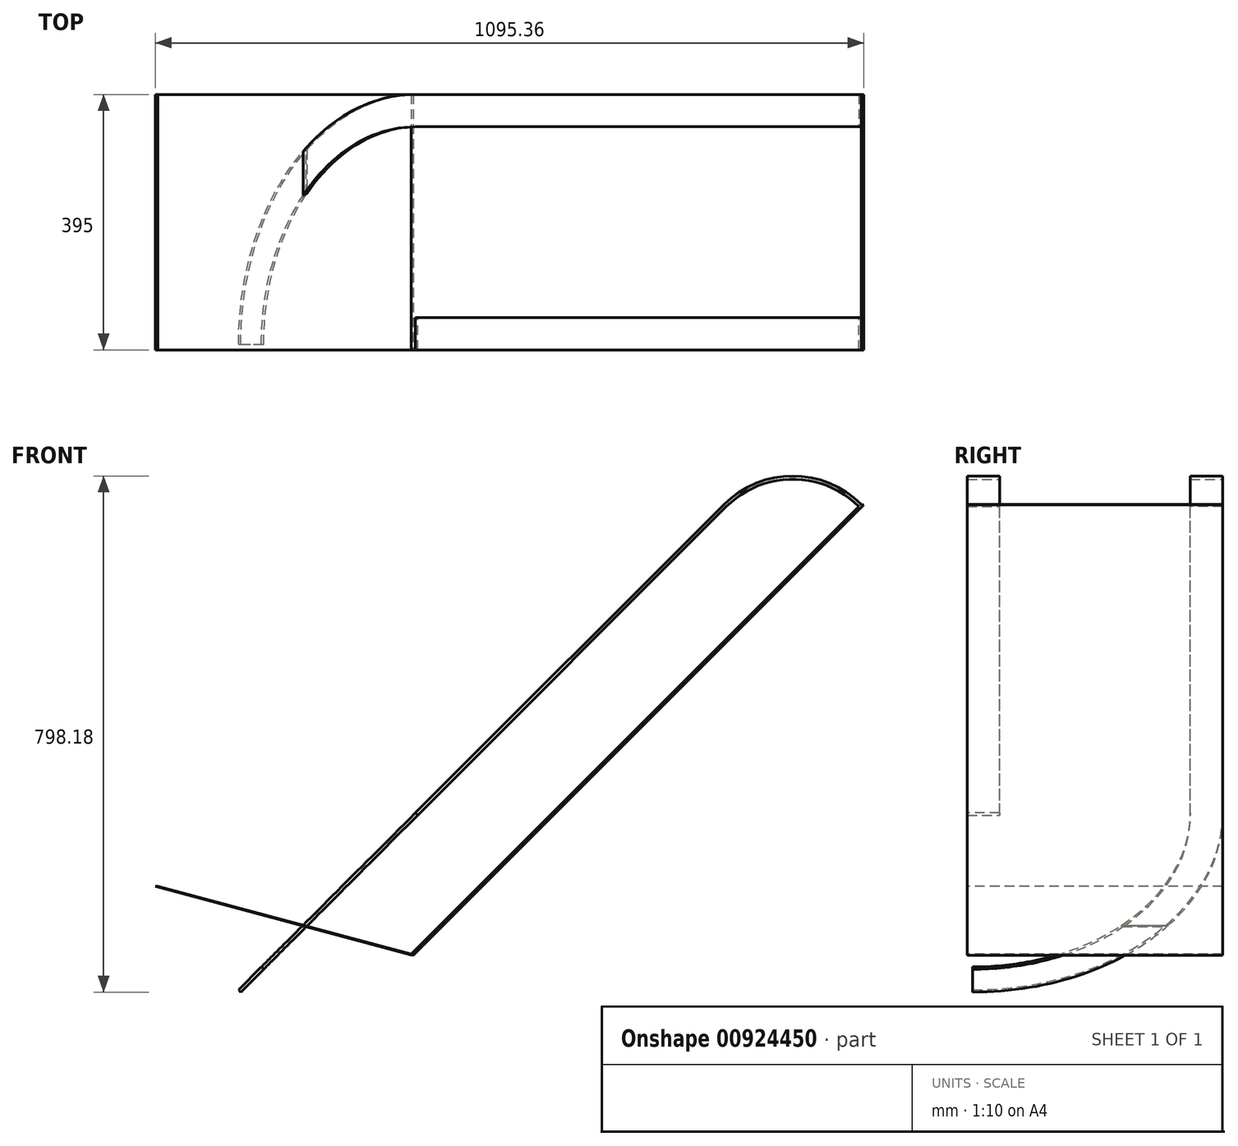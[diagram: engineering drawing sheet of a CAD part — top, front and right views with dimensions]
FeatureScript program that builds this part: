
annotation { "Feature Type Name" : "Feature", "Feature Type Description" : "" }
export const myFeature = defineFeature(function(context is Context, id is Id, definition is map)
    precondition{}
    {
        {
            var Q0;
            Q0=qCreatedBy(makeId("Top.planeOp"),FACE);
            var sketch = newSketch(context, id + "F0", { "sketchPlane" : qUnion([Q0])});
            skLineSegment(sketch, "E0.bottom", {"start": v(-2, 197.5) * mm, "end": v(2, 197.5) * mm});
            skLineSegment(sketch, "E0.top", {"start": v(-2, -197.5) * mm, "end": v(2, -197.5) * mm});
            skLineSegment(sketch, "E0.left", {"start": v(-2, 197.5) * mm, "end": v(-2, -197.5) * mm});
            skLineSegment(sketch, "E0.right", {"start": v(2, 197.5) * mm, "end": v(2, -197.5) * mm});
            skSolve(sketch);
        }
        {
            var Q0;
            Q0=qCreatedBy(makeId("Front.planeOp"),FACE);
            var sketch = newSketch(context, id + "F1", { "sketchPlane" : qUnion([Q0])});
            skLineSegment(sketch, "E1", {"start": v(-186.53, 48.88) * mm, "end": v(208.47, -56.96) * mm});
            skSolve(sketch);
        }
        {
            var Q0;
            Q0=makeQuery(id+"F0.imprint","IMPRINT",FACE,{"disambiguationData":[TD([[makeQuery(id+"F0.imprint","IMPRINT",EDGE,{"derivedFrom":sQuery(id+"F0.wireOp",EDGE,"E0.bottom")}),-1.0]])]});
            var Q1;
            Q1=sQuery(id+"F1.wireOp",EDGE,"E1");
            sweep(context, id + "F2", {"profiles" : qUnion([Q0]), "path" : qUnion([Q1])});
        }
        {
            var Q0;
            Q0=makeQuery(id+"F2.opSweep","SWEPT_FACE",FACE,{"disambiguationData":[OSD([sQuery(id+"F0.wireOp",EDGE,"E0.left"),sQuery(id+"F1.wireOp",EDGE,"E1")])]});
            var sketch = newSketch(context, id + "F3", { "sketchPlane" : qUnion([Q0])});
            skLineSegment(sketch, "E2.bottom", {"start": v(222.14, -197.5) * mm, "end": v(218.14, -197.5) * mm});
            skLineSegment(sketch, "E2.top", {"start": v(222.14, 197.5) * mm, "end": v(218.14, 197.5) * mm});
            skLineSegment(sketch, "E2.left", {"start": v(222.14, -197.5) * mm, "end": v(222.14, 197.5) * mm});
            skLineSegment(sketch, "E2.right", {"start": v(218.14, -197.5) * mm, "end": v(218.14, 197.5) * mm});
            skSolve(sketch);
        }
        {
            var Q0;
            Q0=qCreatedBy(makeId("Front.planeOp"),FACE);
            var sketch = newSketch(context, id + "F4", { "sketchPlane" : qUnion([Q0])});
            skLineSegment(sketch, "E3", {"start": v(214.23, -57.94) * mm, "end": v(910.73, 638.56) * mm});
            skSolve(sketch);
        }
        {
            var Q0;
            Q0=qSketchRegion(id+"F3",true);
            var Q1;
            Q1=sQuery(id+"F4.wireOp",EDGE,"E3");
            sweep(context, id + "F5", {"operationType" : NewBodyOperationType.ADD, "profiles" : qUnion([Q0]), "path" : qUnion([Q1])});
        }
        {
            var Q0;
            Q0=makeQuery(id+"F5.opSweep","SWEPT_FACE",FACE,{"disambiguationData":[OSD([sQuery(id+"F3.wireOp",EDGE,"E2.right"),sQuery(id+"F4.wireOp",EDGE,"E3")])]});
            var sketch = newSketch(context, id + "F6", { "sketchPlane" : qUnion([Q0])});
            skLineSegment(sketch, "E4.bottom", {"start": v(-197.5, 1093.62) * mm, "end": v(-147.5, 1093.62) * mm});
            skLineSegment(sketch, "E4.top", {"start": v(-197.5, 1088.62) * mm, "end": v(-147.5, 1088.62) * mm});
            skLineSegment(sketch, "E4.left", {"start": v(-197.5, 1093.62) * mm, "end": v(-197.5, 1088.62) * mm});
            skLineSegment(sketch, "E4.right", {"start": v(-147.5, 1093.62) * mm, "end": v(-147.5, 1088.62) * mm});
            skLineSegment(sketch, "E5.bottom", {"start": v(197.5, 1093.62) * mm, "end": v(147.5, 1093.62) * mm});
            skLineSegment(sketch, "E5.top", {"start": v(197.5, 1088.62) * mm, "end": v(147.5, 1088.62) * mm});
            skLineSegment(sketch, "E5.left", {"start": v(197.5, 1093.62) * mm, "end": v(197.5, 1088.62) * mm});
            skLineSegment(sketch, "E5.right", {"start": v(147.5, 1093.62) * mm, "end": v(147.5, 1088.62) * mm});
            skLineSegment(sketch, "E6", {"start": v(-366.75, 943.62) * mm, "end": v(490.08, 943.62) * mm});
            skSolve(sketch);
        }
        {
            var Q0;
            Q0=qSketchRegion(id+"F6",true);
            var Q1;
            Q1=sQuery(id+"F6.wireOp",EDGE,"E6");
            revolve(context, id + "F7", {"operationType" : NewBodyOperationType.ADD, "surfaceOperationType" : NewSurfaceOperationType.NEW, "entities" : qUnion([Q0]), "axis" : qUnion([Q1]), "revolveType" : RevolveType.ONE_DIRECTION, "angle" : 90 * degree});
        }
        {
            var Q0;
            Q0=makeQuery(id+"F7.opRevolve","CAP_FACE",FACE,{"disambiguationData":[OSD([sQuery(id+"F6.wireOp",EDGE,"E5.bottom"),sQuery(id+"F6.wireOp",EDGE,"E5.top"),sQuery(id+"F6.wireOp",EDGE,"E5.left"),sQuery(id+"F6.wireOp",EDGE,"E5.right")])],"isStart":false});
            var Q1;
            Q1=makeQuery(id+"F7.opRevolve","CAP_FACE",FACE,{"disambiguationData":[OSD([sQuery(id+"F6.wireOp",EDGE,"E4.bottom"),sQuery(id+"F6.wireOp",EDGE,"E4.top"),sQuery(id+"F6.wireOp",EDGE,"E4.left"),sQuery(id+"F6.wireOp",EDGE,"E4.right")])],"isStart":false});
            extrude(context, id + "F8", {"entities" : qUnion([Q0, Q1]), "operationType" : NewBodyOperationType.ADD, "depth" : 675 * mm, "offsetDistance" : 25 * mm});
        }
        {
            var Q0;
            Q0=makeQuery(id+"F8.opExtrude","CAP_FACE",FACE,{"disambiguationData":[OSD([sQuery(id+"F6.wireOp",EDGE,"E5.bottom"),sQuery(id+"F6.wireOp",EDGE,"E5.top"),sQuery(id+"F6.wireOp",EDGE,"E5.left"),sQuery(id+"F6.wireOp",EDGE,"E5.right")])],"isStart":false});
            var sketch = newSketch(context, id + "F9", { "sketchPlane" : qUnion([Q0])});
            skLineSegment(sketch, "E7", {"start": v(189.17, 242.66) * mm, "end": v(189.17, -277.16) * mm});
            skSolve(sketch);
        }
        {
            var Q0;
            Q0=makeQuery(id+"F9.imprint","IMPRINT",FACE,{"disambiguationData":[TD([[makeQuery(id+"F9.imprint","IMPRINT",EDGE,{"derivedFrom":makeQuery(id+"F8.opExtrude","CAP_EDGE",EDGE,{"disambiguationData":[OSD([sQuery(id+"F6.wireOp",EDGE,"E5.bottom")])],"isStart":false})}),-1.0]])]});
            var Q1;
            Q1=makeQuery(id+"F8.opExtrude","CAP_FACE",FACE,{"disambiguationData":[OSD([sQuery(id+"F6.wireOp",EDGE,"E4.bottom"),sQuery(id+"F6.wireOp",EDGE,"E4.top"),sQuery(id+"F6.wireOp",EDGE,"E4.left"),sQuery(id+"F6.wireOp",EDGE,"E4.right")])],"isStart":false});
            var Q2;
            Q2=sQuery(id+"F9.wireOp",EDGE,"E7");
            revolve(context, id + "F10", {"operationType" : NewBodyOperationType.ADD, "surfaceOperationType" : NewSurfaceOperationType.NEW, "entities" : qUnion([Q0, Q1]), "axis" : qUnion([Q2]), "revolveType" : RevolveType.ONE_DIRECTION, "oppositeDirection" : true, "angle" : 90 * degree});
        }
    });
